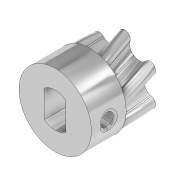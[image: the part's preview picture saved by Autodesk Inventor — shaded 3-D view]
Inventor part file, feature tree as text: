
AUTODESK INVENTOR PART (.ipt)
format: ipt  version: 2020 (Build 240168000, 168)  size: 547,328 bytes
history: native  units: in
note: dims shown in document units (in); Inventor stores cm internally (conversion verified against a paired STEP export)
features: sketch x9, extrude x4, sweep x2, projected_geometry x2, fillet x1, other x1
ambient origin geometry x8: Origin, YZ Plane, XZ Plane, XY Plane, X Axis, Y Axis, Z Axis, Center Point
bodies: Solid1 (feature_tree)
feature tree (19):
  sweep  "Sweep1"
  sketch  "3D Sketch2"
  extrude  "Extrusion1"  Depth=0.0787in
  extrude  "Extrusion2"  Depth=0.0787in
  fillet  "Fillet1"  Radius=2.3622in
  sweep  "Sweep2"
  extrude  "Extrusion3"  Depth=0.0748in
  extrude  "Extrusion4"  Depth=0.122in
  sketch  "Sketch1"  dims[d0=0.1969in d1=0.4094in]
  sketch  "3D Sketch1"
  other  "Helical Curve1"
  sketch  "Sketch2"  dims[d2=0.0866in d3=0.0787in]
  projected_geometry  "Projected Loop1"
  sketch  "Sketch3"  dims[d4=0.0787in d5=0.0787in d6=2.3622in d8=360.0deg]
  sketch  "Sketch4"  dims[d10=0.1969in d11=0.0236in d12=0.236in d13=0.0in d14=0.0in d15=0.0in]
  projected_geometry  "Projected Loop2"
  sketch  "3D Sketch3"
  sketch  "Sketch5"  dims[d16=0.1969in d17=0.0in d18=0.0748in]
  sketch  "Sketch6"  dims[d19=0.205in d20=0.0in d21=0.0118in d22=0.0079in d23=0.0in d24=0.0in d29=0.0039in d30=0.1969in d31=0.0in d32=0.122in d33=0.061in d34=1.0in d35=0.0in]
